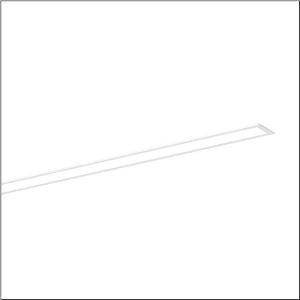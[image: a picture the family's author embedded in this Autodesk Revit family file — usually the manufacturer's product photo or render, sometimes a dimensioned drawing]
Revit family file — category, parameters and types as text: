
# Revit family: silica_21_51mx10dn35wb
name_source: partatom
category: Lighting Fixtures
units: mm (PartAtom-declared; Revit-internal decimal feet)

## family parameters
Cut with Voids When Loaded = No
Host = Face
Light Source = No
Part Type = Normal
Room Calculation Point = No
Round Connector Dimension = Use Diameter
Shared = No

## types (1)
- --- (1 x LED, 5400 lm, 37.4 W, 3000K)
    Apparent Load = 37 VA
    CIE Flux Codes = 48 79 96 100 100
    Color Rendering = 80
    Color Temperature = 3000K
    Default Elevation = 1800 mm
    Description = Silica 21, office luminaire, primary optical cover: prismatic diffuser, of PMMA, CAT 2 (L<= 3000cd/m²), light emission: direct distribution, primary light characteristic: symmetric, installation type: recessed, LED, rated luminous flux: 5.400lm, luminous efficacy: 144lm/W, light colour: 830, colour temperature: 3000K, control gear: DALI 2, with terminal, 3+2-pole, max. 2.5mm², mains connection: 220..240V, AC, 50/60Hz, rated input power: 37.4W, luminaire housing, of aluminium, traffic white (RAL 9016), length: 2.728mm, width: 79mm, height: 53mm, protection rating (complete): IP20, insulation class (complete): insulation class I (protective earthing), certification: CE, ENEC, VDE, permissible operating ambient temperature: 0..+35°C, standard: EN 50419, packaging unit: 1 piece
    Height = 0 mm  [stored 0 ft]
    Lamp = 1 x LED
    Lamp Light Flux = 5400 lm
    Lamp Power = 37.4 W
    Lamp count = 1
    Length = 2727 mm
    Luminous efficacy = 144 lm/W
    Manufacturer = Siteco
    ModVariant = No
    Model = 51MX10DN35WB
    Mounting Place = Ceiling
    Mounting Type = Recessed
    Number of Poles = 1
    OnlyDefault = Yes
    Power Factor = 1
    Product Name = Silica 21
    Product group = office luminaire | ceiling recessed
    ProductGroupID = 400
    Protection Class = Protection class I
    Protection Degree = IP 20
    RLX_Detail_Level = 1
    RLX_Emergency_Light_Flux = 0 lm
    RLX_Emergency_Type = 0
    RLX_Emergency_Type_DB = No
    RlxData = <blob elided: 21461 chars, md5=0f0af1fc>
    Socket = socket
    Standby Power = 0 W
    System Light Flux = 5400 lm
    System Power = 37 W
    Type Comments = factory setting: luminous flux: 100 % | dim-lin: 254 | 233 mA
    Type Image = l_1335891.jpg
    URL = http://relux.com
    VarID = @adj_071811
    Voltage = 0 V
    Weight = 0.00 kg
    Width = 79 mm

note: [stored X ft] marks values corroborated as IEEE doubles in the binary element streams (Revit-internal decimal feet)

## geometry (parser evidence)
native form markers: Blend x4, Sweep x9
no freeform markers — native parametric forms only
